# Revit family: Shelf-Recessed-Whitehall-BestCare-WH1820FA_Series
name_source: partatom
category: Specialty Equipment
revit_build: Autodesk Revit 2018 (Build: 20170223_1515(x64)
units: mm (PartAtom-declared; Revit-internal decimal feet)

## family parameters
Cut with Voids When Loaded = Yes
Host = Face
OmniClass Number = 23.40.20.27.11
OmniClass Title = Shelves
Part Type = Normal
Room Calculation Point = No
Round Connector Dimension = Use Diameter
Shared = Yes

## types (2) — shared parameters
ADA Compliant = Yes
Assembly Code = C1030320
Default Elevation = 0"
Description = BestCare® Ligature-Resistant Recessed Shelf
Height = 8"
Inner Length = 16"
Inner Width = 5"
Installation Type = Recessed Wall Mounted
Length = 19"
Manufacturer = Whitehall Mfg.
Price = Prices may vary. Please consult Manufacturer Representative for most up-to-date price list.
Product Documentation Link = https://www.whitehallmfg.com
Product Page URL = https://www.whitehallmfg.com
URL = https://www.whitehallmfg.com
Width = 4"

## per-type parameters (varying)
| type | Finish | Material |
| WH1820FA | Enviro Glaze-Whitehall-Powder Coated Snow White | Enviro Glaze-Whitehall-Powder Coated Snow White |
| WH1820FA-SS | Metal-Whitehall-Stainless Steel | Metal-Whitehall-Stainless Steel |

note: column(s) folded — value = type name in every type: Model

## geometry (parser evidence)
native form markers: Sweep x3
no freeform markers — native parametric forms only
